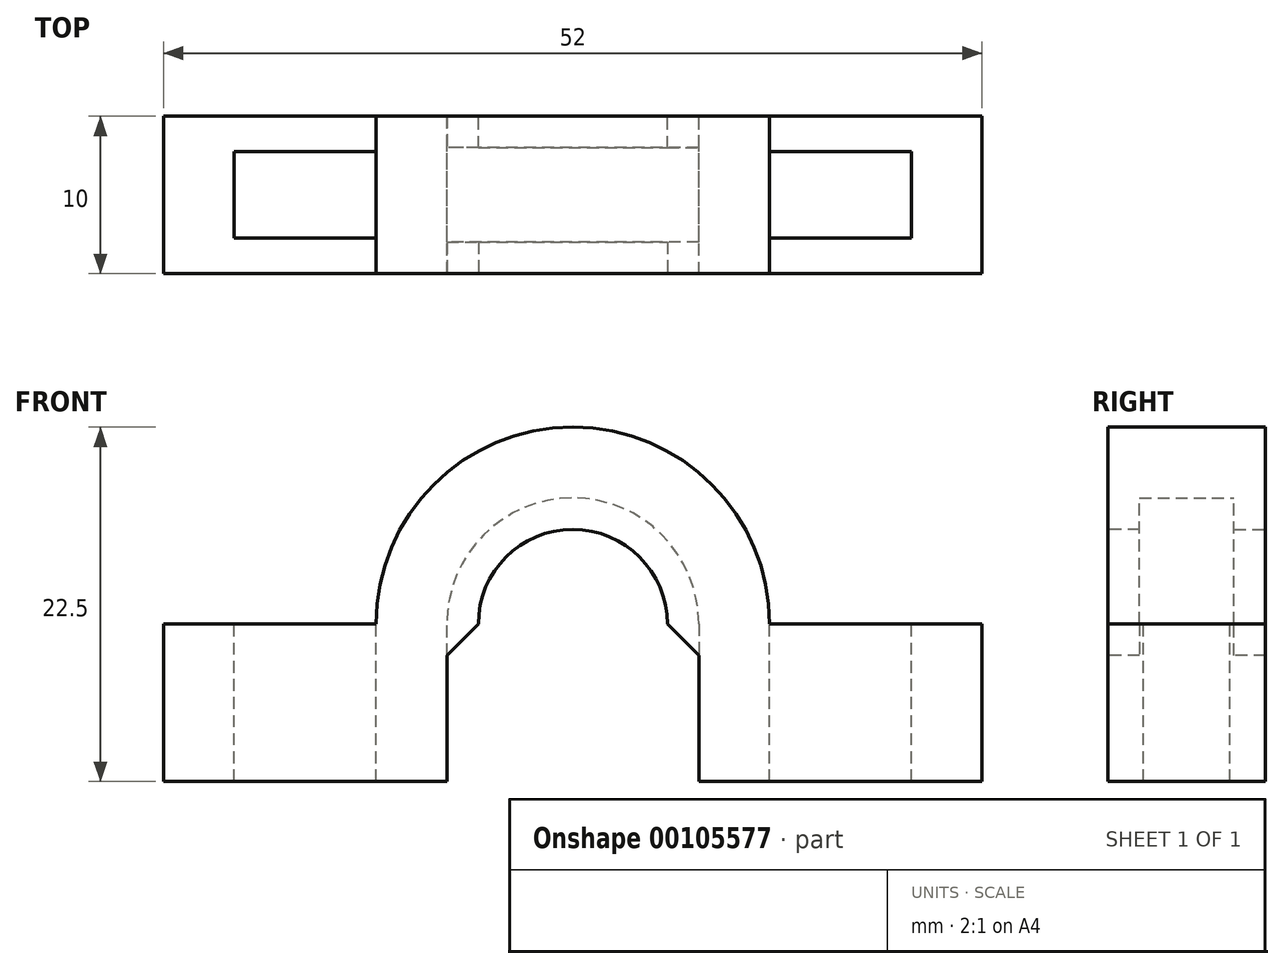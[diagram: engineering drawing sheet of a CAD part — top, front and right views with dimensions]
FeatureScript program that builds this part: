
annotation { "Feature Type Name" : "Feature", "Feature Type Description" : "" }
export const myFeature = defineFeature(function(context is Context, id is Id, definition is map)
    precondition{}
    {
        {
            var Q0;
            Q0=qCreatedBy(makeId("Front.planeOp"),FACE);
            var sketch = newSketch(context, id + "F0", { "sketchPlane" : qUnion([Q0])});
            skArc(sketch, "E0", {"start": v(12.5, 0) * mm, "mid": v(0, 12.5) * mm, "end": v(-12.5, 0) * mm});
            skArc(sketch, "E1", {"start": v(8, 0) * mm, "mid": v(0, 8) * mm, "end": v(-8, 0) * mm});
            skLineSegment(sketch, "E2", {"start": v(-12.5, 0) * mm, "end": v(-8, 0) * mm});
            skLineSegment(sketch, "E3.trimOffspring", {"start": v(8, 0) * mm, "end": v(12.5, 0) * mm});
            skLineSegment(sketch, "E4.bottom", {"start": v(-8, 0) * mm, "end": v(-26, 0) * mm});
            skLineSegment(sketch, "E4.top", {"start": v(-8, -10) * mm, "end": v(-26, -10) * mm});
            skLineSegment(sketch, "E4.left", {"start": v(-8, 0) * mm, "end": v(-8, -10) * mm});
            skLineSegment(sketch, "E4.right", {"start": v(-26, 0) * mm, "end": v(-26, -10) * mm});
            skLineSegment(sketch, "E5.MirrorCS", {"start": v(12.5, 0) * mm, "end": v(8, 0) * mm});
            skLineSegment(sketch, "E6.MirrorCS", {"start": v(8, -10) * mm, "end": v(26, -10) * mm});
            skLineSegment(sketch, "E7.MirrorCS", {"start": v(8, 0) * mm, "end": v(8, -10) * mm});
            skLineSegment(sketch, "E8.MirrorCS", {"start": v(8, 0) * mm, "end": v(26, 0) * mm});
            skLineSegment(sketch, "E9.MirrorCS", {"start": v(26, 0) * mm, "end": v(26, -10) * mm});
            skPoint(sketch, "E10.MirrorCS.start.orphan", {"position": v(-8, 0) * mm});
            skPoint(sketch, "E11.MirrorCS.start.orphan", {"position": v(-12.5, 0) * mm});
            skSolve(sketch);
        }
        {
            var Q0;
            Q0 = qSketchRegion(id + "F0", true);
            extrude(context, id + "F1", {"entities" : qUnion([Q0]), "depth" : 5 * mm, "hasSecondDirection" : true, "secondDirectionOppositeDirection" : true, "secondDirectionDepth" : 5 * mm});
        }
        {
            var Q0;
            Q0=makeQuery(id+"F1.opExtrude","CAP_FACE",FACE,{"disambiguationData":[OSD([sQuery(id+"F0.wireOp",EDGE,"E0"),sQuery(id+"F0.wireOp",EDGE,"E1"),sQuery(id+"F0.wireOp",EDGE,"E2"),sQuery(id+"F0.wireOp",EDGE,"E3.trimOffspring")])],"isStart":true});
            var sketch = newSketch(context, id + "F2", { "sketchPlane" : qUnion([Q0])});
            skArc(sketch, "E12", {"start": v(8, 0) * mm, "mid": v(0, 8) * mm, "end": v(-8, 0) * mm});
            skArc(sketch, "E13", {"start": v(6, 0) * mm, "mid": v(0, 6) * mm, "end": v(-6, 0) * mm});
            skLineSegment(sketch, "E14", {"start": v(-8, 0) * mm, "end": v(-6, 0) * mm});
            skLineSegment(sketch, "E15", {"start": v(6, 0) * mm, "end": v(8, 0) * mm});
            skSolve(sketch);
        }
        {
            var Q0;
            Q0 = qSketchRegion(id + "F2", true);
            extrude(context, id + "F3", {"entities" : qUnion([Q0]), "operationType" : NewBodyOperationType.ADD, "oppositeDirection" : true, "depth" : 2 * mm});
        }
        {
            var Q0;
            Q0=makeQuery(id+"F1.opExtrude","SWEPT_BODY",BODY,{"disambiguationData":[OSD([sQuery(id+"F0.wireOp",EDGE,"E0"),sQuery(id+"F0.wireOp",EDGE,"E1"),sQuery(id+"F0.wireOp",EDGE,"E4.bottom"),sQuery(id+"F0.wireOp",EDGE,"E4.top"),sQuery(id+"F0.wireOp",EDGE,"E4.left"),sQuery(id+"F0.wireOp",EDGE,"E4.right"),sQuery(id+"F0.wireOp",EDGE,"E6.MirrorCS"),sQuery(id+"F0.wireOp",EDGE,"E7.MirrorCS"),sQuery(id+"F0.wireOp",EDGE,"E8.MirrorCS"),sQuery(id+"F0.wireOp",EDGE,"E9.MirrorCS")])]});
            var Q1;
            Q1=qCreatedBy(makeId("Front.planeOp"),FACE);
            mirror(context, id + "F4", {"operationType" : NewBodyOperationType.ADD, "entities" : qUnion([Q0]), "mirrorPlane" : qUnion([Q1])});
        }
        {
            var Q0;
            Q0=makeQuery(id+"F1.opExtrude","SWEPT_FACE",FACE,{"disambiguationData":[OSD([sQuery(id+"F0.wireOp",EDGE,"E8.MirrorCS")])]});
            var sketch = newSketch(context, id + "F5", { "sketchPlane" : qUnion([Q0])});
            skLineSegment(sketch, "E16.bottom", {"start": v(-12.5, -2.75) * mm, "end": v(-21.5, -2.75) * mm});
            skLineSegment(sketch, "E16.top", {"start": v(-12.5, 2.75) * mm, "end": v(-21.5, 2.75) * mm});
            skLineSegment(sketch, "E16.left", {"start": v(-12.5, -2.75) * mm, "end": v(-12.5, 2.75) * mm});
            skLineSegment(sketch, "E16.right", {"start": v(-21.5, -2.75) * mm, "end": v(-21.5, 2.75) * mm});
            skPoint(sketch, "E16.middle", {"position": v(-17, 0) * mm});
            skLineSegment(sketch, "E17.MirrorCS", {"start": v(12.5, -2.75) * mm, "end": v(21.5, -2.75) * mm});
            skLineSegment(sketch, "E18.MirrorCS", {"start": v(21.5, -2.75) * mm, "end": v(21.5, 2.75) * mm});
            skLineSegment(sketch, "E19.MirrorCS", {"start": v(12.5, -2.75) * mm, "end": v(12.5, 2.75) * mm});
            skPoint(sketch, "E20.MirrorP", {"position": v(17, 0) * mm});
            skLineSegment(sketch, "E21.MirrorCS", {"start": v(12.5, 2.75) * mm, "end": v(21.5, 2.75) * mm});
            skSolve(sketch);
        }
        {
            var Q0;
            Q0 = qSketchRegion(id + "F5", true);
            extrude(context, id + "F6", {"entities" : qUnion([Q0]), "operationType" : NewBodyOperationType.REMOVE, "oppositeDirection" : true, "depth" : 25 * mm});
        }
        {
            var Q0;
            {var subQ0=sQuery(id+"F0.wireOp",EDGE,"E4.left");var subQ1=makeQuery(id+"F1.opExtrude","SWEPT_EDGE",EDGE,{"disambiguationData":[OSD([sQuery(id+"F0.wireOp",EDGE,"E1"),sQuery(id+"F0.wireOp",EDGE,"E4.bottom"),subQ0])]});Q0=makeQuery(id+"F4.boolean.opBoolean","MERGE",EDGE,{"derivedFrom":[makeQuery(id+"F3.boolean.opBoolean","SPLIT",EDGE,{"derivedFrom":subQ1}),makeQuery(id+"F4.opPattern","COPY",EDGE,{"derivedFrom":makeQuery(id+"F3.boolean.opBoolean","MERGE",EDGE,{"derivedFrom":[subQ1,makeQuery(id+"F3.opExtrude","SWEPT_EDGE",EDGE,{"disambiguationData":[OSD([subQ0,sQuery(id+"F2.wireOp",EDGE,"E12"),sQuery(id+"F2.wireOp",EDGE,"E15")])]})]}),"instanceName":"1"})]});}
            var Q1;
            {var subQ0=sQuery(id+"F0.wireOp",EDGE,"E4.left");Q1=makeQuery(id+"F3.boolean.opBoolean","MERGE",EDGE,{"derivedFrom":[makeQuery(id+"F1.opExtrude","SWEPT_EDGE",EDGE,{"disambiguationData":[OSD([sQuery(id+"F0.wireOp",EDGE,"E1"),sQuery(id+"F0.wireOp",EDGE,"E4.bottom"),subQ0])]}),makeQuery(id+"F3.opExtrude","SWEPT_EDGE",EDGE,{"disambiguationData":[OSD([subQ0,sQuery(id+"F2.wireOp",EDGE,"E12"),sQuery(id+"F2.wireOp",EDGE,"E15")])]})]});}
            var Q2;
            {var subQ0=sQuery(id+"F0.wireOp",EDGE,"E7.MirrorCS");var subQ1=makeQuery(id+"F1.opExtrude","SWEPT_EDGE",EDGE,{"disambiguationData":[OSD([sQuery(id+"F0.wireOp",EDGE,"E1"),subQ0,sQuery(id+"F0.wireOp",EDGE,"E8.MirrorCS")])]});Q2=makeQuery(id+"F4.boolean.opBoolean","MERGE",EDGE,{"derivedFrom":[makeQuery(id+"F3.boolean.opBoolean","SPLIT",EDGE,{"derivedFrom":subQ1}),makeQuery(id+"F4.opPattern","COPY",EDGE,{"derivedFrom":makeQuery(id+"F3.boolean.opBoolean","MERGE",EDGE,{"derivedFrom":[subQ1,makeQuery(id+"F3.opExtrude","SWEPT_EDGE",EDGE,{"disambiguationData":[OSD([subQ0,sQuery(id+"F2.wireOp",EDGE,"E12"),sQuery(id+"F2.wireOp",EDGE,"E14")])]})]}),"instanceName":"1"})]});}
            var Q3;
            {var subQ0=sQuery(id+"F0.wireOp",EDGE,"E7.MirrorCS");Q3=makeQuery(id+"F3.boolean.opBoolean","MERGE",EDGE,{"derivedFrom":[makeQuery(id+"F1.opExtrude","SWEPT_EDGE",EDGE,{"disambiguationData":[OSD([sQuery(id+"F0.wireOp",EDGE,"E1"),subQ0,sQuery(id+"F0.wireOp",EDGE,"E8.MirrorCS")])]}),makeQuery(id+"F3.opExtrude","SWEPT_EDGE",EDGE,{"disambiguationData":[OSD([subQ0,sQuery(id+"F2.wireOp",EDGE,"E12"),sQuery(id+"F2.wireOp",EDGE,"E14")])]})]});}
            chamfer(context, id + "F7", {"entities" : qUnion([Q0, Q1, Q2, Q3]), "width" : 2 * mm, "tangentPropagation" : true});
        }
    });
